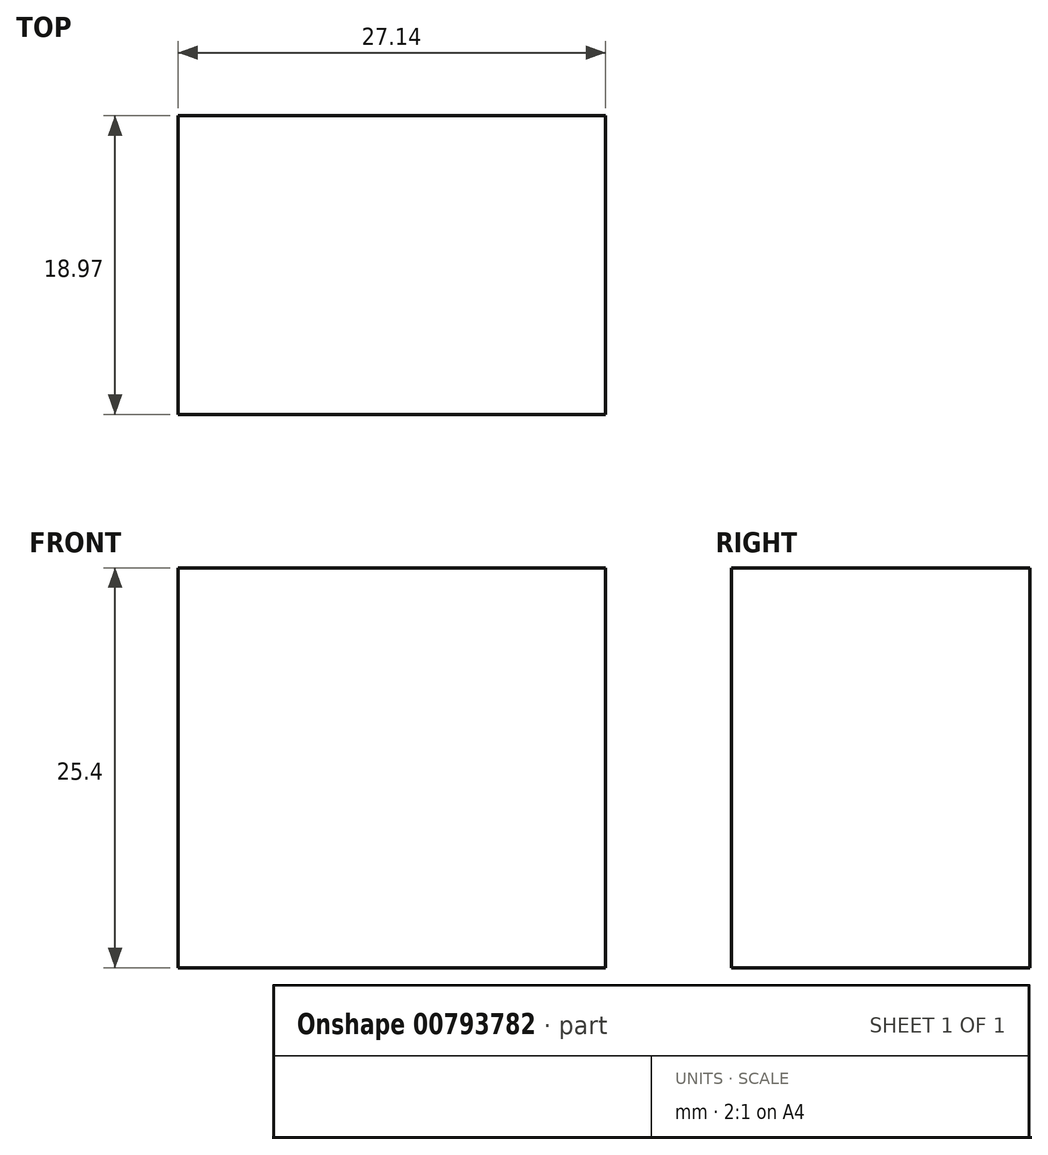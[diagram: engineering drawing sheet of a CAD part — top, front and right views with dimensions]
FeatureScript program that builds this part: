
annotation { "Feature Type Name" : "Feature", "Feature Type Description" : "" }
export const myFeature = defineFeature(function(context is Context, id is Id, definition is map)
    precondition{}
    {
        {
            var Q0;
            Q0=qCreatedBy(makeId("Top.planeOp"),FACE);
            var sketch = newSketch(context, id + "F0", { "sketchPlane" : qUnion([Q0])});
            skLineSegment(sketch, "E0.bottom", {"start": v(0, 0) * mm, "end": v(27.14, 0) * mm});
            skLineSegment(sketch, "E0.top", {"start": v(0, -18.97) * mm, "end": v(27.14, -18.97) * mm});
            skLineSegment(sketch, "E0.left", {"start": v(0, 0) * mm, "end": v(0, -18.97) * mm});
            skLineSegment(sketch, "E0.right", {"start": v(27.14, 0) * mm, "end": v(27.14, -18.97) * mm});
            skSolve(sketch);
        }
        {
            var Q0;
            Q0=makeQuery(id+"F0.imprint","IMPRINT",FACE,{"disambiguationData":[TD([[makeQuery(id+"F0.imprint","IMPRINT",EDGE,{"derivedFrom":sQuery(id+"F0.wireOp",EDGE,"E0.bottom")}),-1.0]])]});
            extrude(context, id + "F1", {"entities" : qUnion([Q0]), "depth" : 25.4 * mm, "offsetDistance" : 25.4 * mm});
        }
    });
